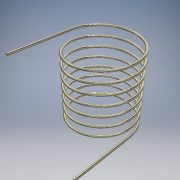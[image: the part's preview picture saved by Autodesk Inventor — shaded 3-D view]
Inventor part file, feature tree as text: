
AUTODESK INVENTOR PART (.ipt)
format: ipt  version: 2017 (Build 210142000, 142)  size: 281,088 bytes
history: native  units: in
note: dims shown in document units (in); Inventor stores cm internally (conversion verified against a paired STEP export)
features: sketch x2, helix x1, extrude x1
ambient origin geometry x8: Origin, YZ Plane, XZ Plane, XY Plane, X Axis, Y Axis, Z Axis, Center Point
bodies: Solid1 (feature_tree)
feature tree (4):
  helix  "Coil1"  [1 undecoded]
  extrude  "Extrusion1"  Depth=0.04in TaperAngle=0.0deg
  sketch  "Sketch1"  dims[d1=0.125in]
  sketch  "Sketch2"  dims[d2=0.04in d3=1.0in d4=2.9528in d5=0.0in d6=90.0deg d7=90.0deg d8=0.0in d9=0.0in d10=0.25in d11=0.0in]
note: 1 required parameter value undecoded (feature->parameter linkage not recoverable at this tier; creation-order binding heuristic only, values carry confidence <= 0.55)
